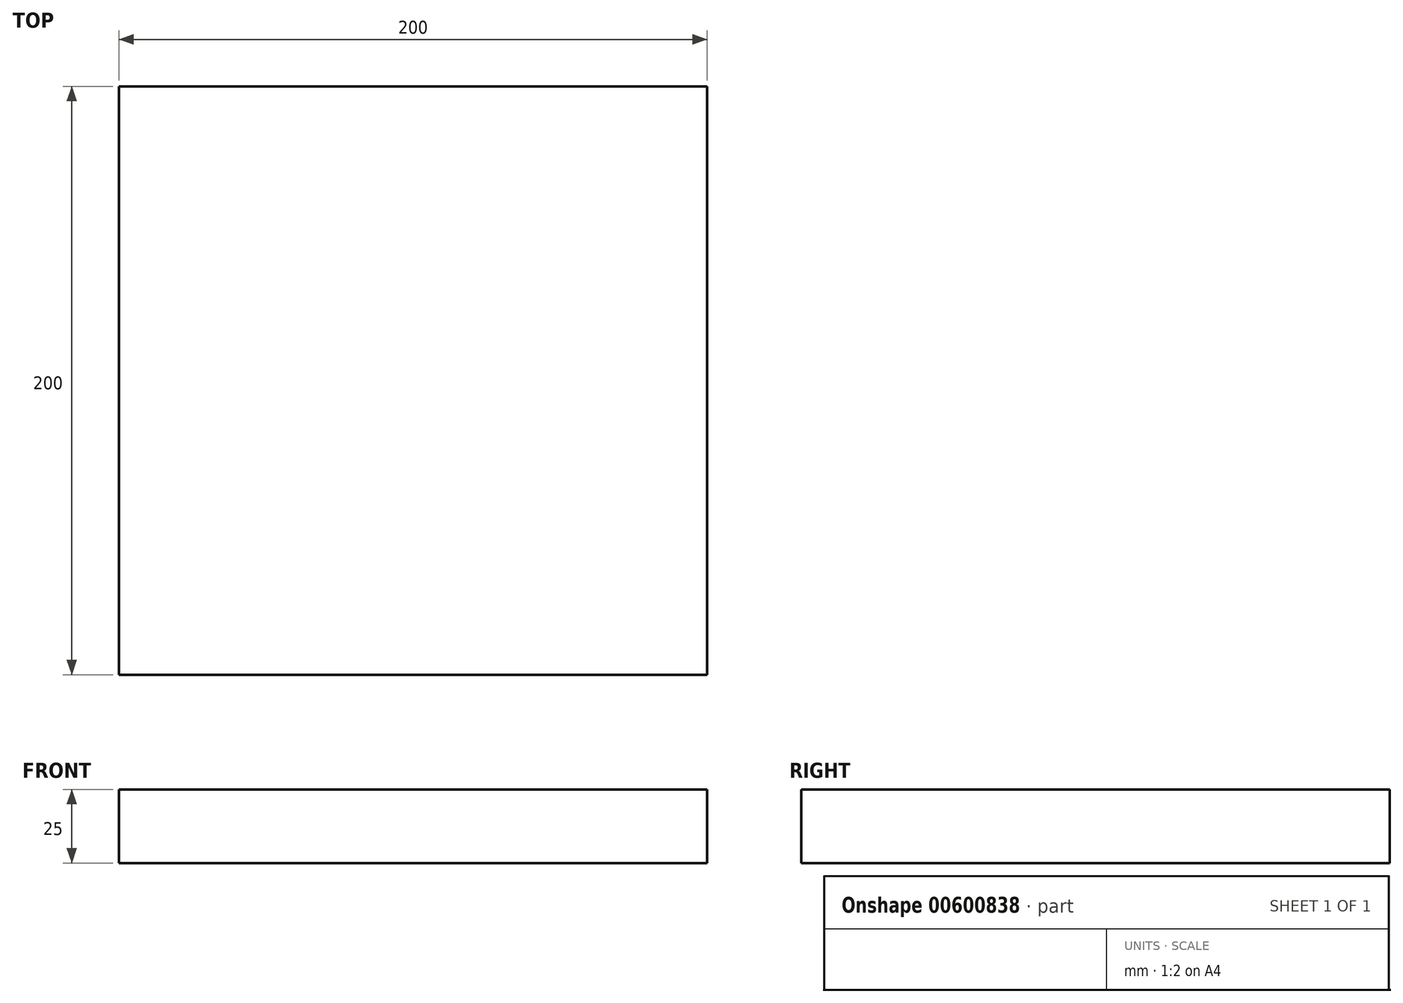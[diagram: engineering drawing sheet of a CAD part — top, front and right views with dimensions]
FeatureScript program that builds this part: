
annotation { "Feature Type Name" : "Feature", "Feature Type Description" : "" }
export const myFeature = defineFeature(function(context is Context, id is Id, definition is map)
    precondition{}
    {
        {
            var Q0;
            Q0=qCreatedBy(makeId("Top.planeOp"),FACE);
            var sketch = newSketch(context, id + "F0", { "sketchPlane" : qUnion([Q0])});
            skLineSegment(sketch, "E0.bottom", {"start": v(0, 0) * mm, "end": v(-200, 0) * mm});
            skLineSegment(sketch, "E0.top", {"start": v(0, 200) * mm, "end": v(-200, 200) * mm});
            skLineSegment(sketch, "E0.left", {"start": v(0, 0) * mm, "end": v(0, 200) * mm});
            skLineSegment(sketch, "E0.right", {"start": v(-200, 0) * mm, "end": v(-200, 200) * mm});
            skSolve(sketch);
        }
        {
            var Q0;
            Q0 = qSketchRegion(id + "F0", true);
            extrude(context, id + "F1", {"entities" : qUnion([Q0]), "depth" : 25 * mm, "offsetDistance" : 25 * mm});
        }
    });
